# Revit family: HVAC_Mechanical-Ventilation_Ice-Air_FCU_Vertical-Concealed
name_source: partatom
category: Mechanical Equipment
revit_build: Autodesk Revit 2015 (Build: 20140606_1530(x64)
units: mm (PartAtom-declared; Revit-internal decimal feet)

## types (7) — shared parameters
Air Supply Depth = 5 "
BIMobject category = Air Conditioning
BIMobject category code = hvac-air-con
BIMobject main category = HVAC
BIMobject main category code = hvac
Brand url = http://www.ice-air.com
Condensate Connection = 0.63 "
Copper Material = Copper - Ice_Air - Orange
Default Elevation = 48 "
Depth = 8.43 "
Description = ICE AIRs concealed vertical fan coil FCVC unit is designed to accommodate large spaces where easy access to the equipment for maintenance purposes is preferred.
Design country = United States
Duct Description = Supply Air
Edition number = 1
Frequency = 60 Hz
Height = 24.75 "
IFC Classification = Heat Exchanger
Inlet/Outlet Connection = 0.5 "
Manufacturer = Ice Air
Manufacturer country = United States
Manufacturer name = Ice Air
Masterformat 2014 Code = 23 82 19
Masterformat 2014 Description = Fan Coil Units
Motor = 115V/60Hz
NBS Reference Code = 65-00-29
NBS Reference Description = Fan Coil Units
OmniClass Code = 23-33 33 11
OmniClass Description = Fan Coil Units
Product Guid = 7ad28f81-b23f-4741-ac48-3351387af845
Product SKU = vertical-concealed-fcu
Product data url = https://bimobject.com
Product family = FCU
Product group = Vertical Concealed
Product url = http://www.ice-air.com
QR code = http://bimobject.com
Steel Material = Steel - Ice_Air - Galvanized
Technical description = http://www.ice-air.com
UNSPSC Code = 4010
URL = http://www.ice-air.com
Uniclass 1.4 Code = JU84
Uniclass 1.4 Description = Heating and cooling coils
Uniclass 2.0 Code = PR-65-00-29
Uniclass 2.0 Description = Fan Coil Units
Uniclass 2015 Code = Pr_60_65_37
Uniclass 2015 Name = Heating and cooling coils
Uniformat II Code = D3090
Uniformat II Description = Other HVAC Systems & Equipment
Voltage = 115 V
Weight Net (Kg) = 0
z 2-pipe = Pipe System : 2-pipe
z 4-pipe = Pipe System : 4-pipe
zero-valued in all types: Nominal height, Nominal width

## per-type parameters (varying)
| type | Air Flow (High) | Air Flow (Low) | Air Flow (Med) | Air Supply Width | Cooling Capacity (High) | Cooling Capacity (Low) | Cooling Capacity (Med) | Heating Capacity (High) | Heating Capacity (Low) | Heating Capacity (Med) | Width | z Type |
| 5FCVC02 | 200 CFM | 100 CFM | 150 CFM | 32 " | 6900.0 Btu/h | 4140.0 Btu/h | 5175.0 Btu/h | 10350.0 Btu/h | 6200.0 Btu/h | 7760.0 Btu/h | 34.52 " | 1 |
| 5FCVC03 | 300 CFM | 150 CFM | 225 CFM | 34 " | 8100.0 Btu/h | 4860.0 Btu/h | 6075.0 Btu/h | 12150.0 Btu/h | 7300.0 Btu/h | 9110.0 Btu/h | 36.77 " | 2 |
| 5FCVC04 | 400 CFM | 200 CFM | 300 CFM | 42 " | 11600.0 Btu/h | 6960.0 Btu/h | 8700.0 Btu/h | 17400.0 Btu/h | 10450.0 Btu/h | 11305.0 Btu/h | 44.77 " | 3 |
| 5FCVC06 | 600 CFM | 300 CFM | 450 CFM | 54 " | 18700.0 Btu/h | 11220.0 Btu/h | 14025.0 Btu/h | 28050.0 Btu/h | 16800.0 Btu/h | 22100.0 Btu/h | 56.13 " | 4 |
| 5FCVC08 | 800 CFM | 400 CFM | 600 CFM | 58 " | 20800.0 Btu/h | 12480.0 Btu/h | 15600.0 Btu/h | 31200.0 Btu/h | 18700.0 Btu/h | 23400.0 Btu/h | 60.53 " | 5 |
| 5FCVC10 | 1000 CFM | 500 CFM | 750 CFM | 74 " | 30700.0 Btu/h | 18420.0 Btu/h | 23025.0 Btu/h | 46050.0 Btu/h | 27600.0 Btu/h | 34540.0 Btu/h | 75.77 " | 6 |
| 5FCVC12 | 1200 CFM | 600 CFM | 900 CFM | 78 " | 34100.0 Btu/h | 20460.0 Btu/h | 25575.0 Btu/h | 51150.0 Btu/h | 30650.0 Btu/h | 38360.0 Btu/h | 79.41 " | 7 |

note: column(s) folded — value = type name in every type: Model

## geometry (parser evidence)
native form markers: Sweep x3
no freeform markers — native parametric forms only
